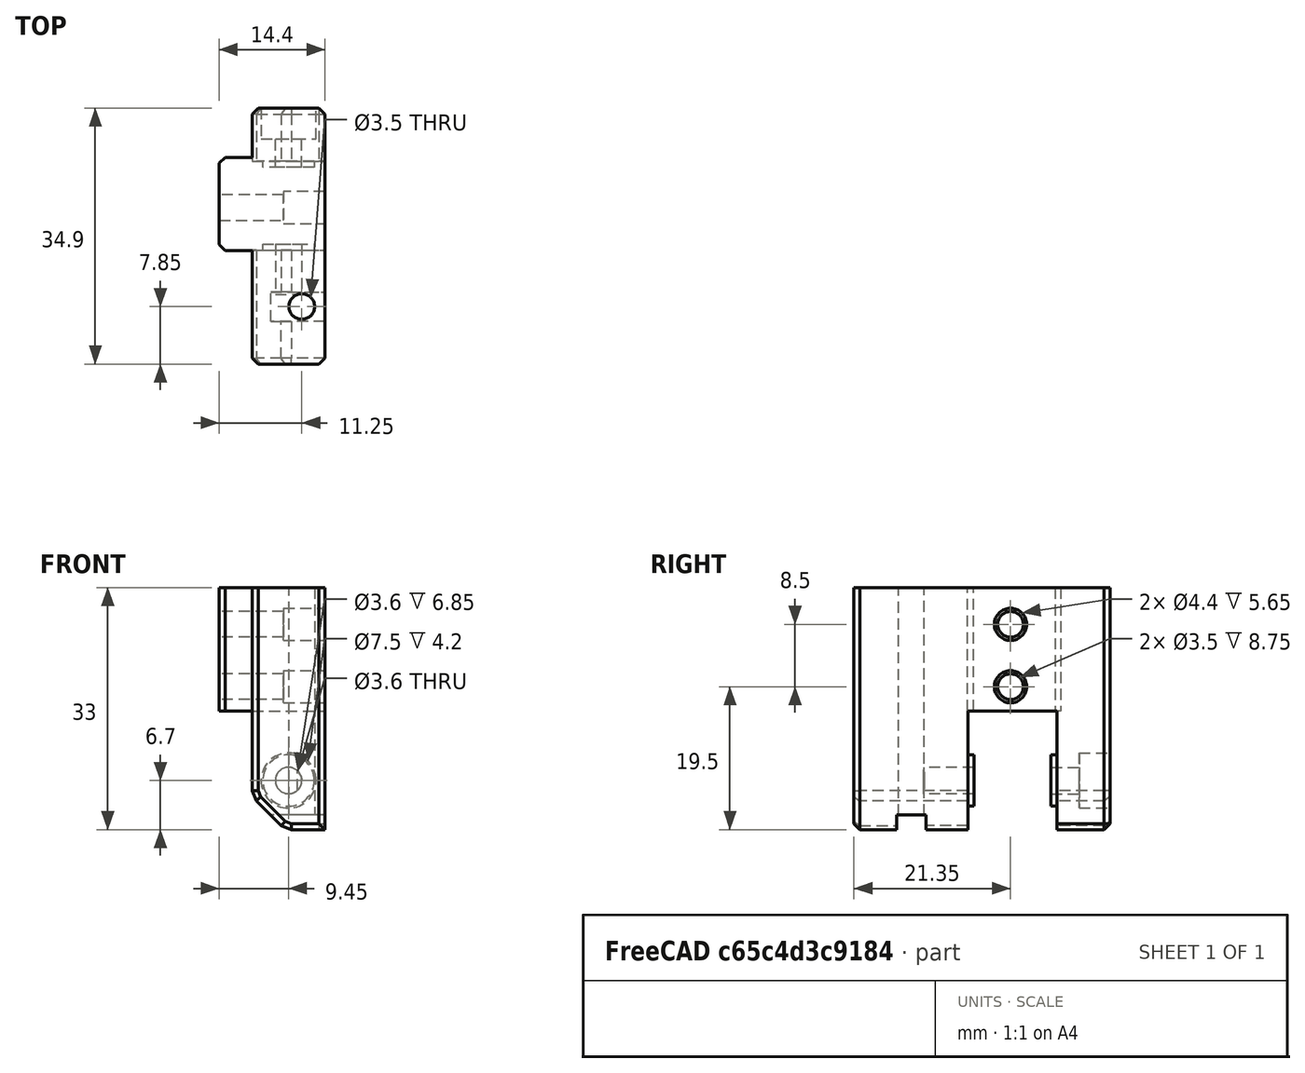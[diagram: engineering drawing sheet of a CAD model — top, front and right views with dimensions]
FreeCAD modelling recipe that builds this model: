
FCSTD DOCUMENT  (FreeCAD 1.0R38641 +468 (Git))
Label: k1_tensioner_left
License: All rights reserved
LicenseURL: https://en.wikipedia.org/wiki/All_rights_reserved
objects: Part::Feature×1, PartDesign::FeatureBase×1, PartDesign::Body×1, App::Link×1, App::Part×1
note: 4 computed .brp shape members not serialized (recipe doc carries the construction recipe); baked Part::Feature solids carry a one-line shape summary decoded from their .brp
EXTERNAL_REF file=cad_powge_pulley.FCStd obj=Part

FEATURE [Part::Feature] Part__Feature  label="step"
  shape: bbox 14.4 x 34.9 x 33 mm, 57 faces (baked)
FEATURE [PartDesign::FeatureBase] BaseFeature
  BaseFeature = -> Part__Feature
  Suppressed = false
FEATURE [PartDesign::Body] Body  label="k1_tensioner_left"
  AllowCompound = false
  BaseFeature = -> Part__Feature
  Group = -> [BaseFeature]
  Origin = -> Origin001
  Tip = -> BaseFeature
FEATURE [App::Link] Link  label="cad_powge_pulley_link"
  LinkPlacement = pos=(5.2,-18.65,6.7) rot=(-1,0,0;1.5708rad)
  LinkedObject = -> <external cad_powge_pulley.FCStd>#Part
  Placement = pos=(5.2,-18.65,6.7) rot=(-1,0,0;1.5708rad)
FEATURE [App::Part] Part  label="k1_tensioner_left_part"
  Group = -> [Body,Link]
  Origin = -> Origin
  Placement = pos=(0,0,0) rot=(0.57735,0.57735,0.57735;2.0944rad)

RESOLVED EXTERNAL PARTS (link-assembly join: the EXTERNAL_REF files above that resolve inside this repo's crawl, each included once):
---- part cad_powge_pulley.FCStd = doc fcstd_d49da9a9e340 ----
FCSTD DOCUMENT  (FreeCAD 1.0R38641 +468 (Git))
Label: cad_powge_pulley
License: All rights reserved
LicenseURL: https://en.wikipedia.org/wiki/All_rights_reserved
objects: Sketcher::SketchObject×1, PartDesign::Revolution×1, PartDesign::Body×1, App::Part×1
note: 6 computed .brp shape members not serialized (recipe doc carries the construction recipe); baked Part::Feature solids carry a one-line shape summary decoded from their .brp

FEATURE [Sketcher::SketchObject] Sketch
  ArcFitTolerance = 1e-06
  AttachmentSupport = -> [XZ_Plane]
  FullyConstrained = true
  MakeInternals = false
  MapMode = 5
  Placement = pos=(0,0,0) rot=(1,0,0;1.5708rad)
  sketch-geometry (8):
    g0: LineSegment StartX=6.1 StartY=9.3 StartZ=0 EndX=6.1 EndY=1.2 EndZ=0
    g1: LineSegment StartX=6.1 StartY=1.2 StartZ=0 EndX=8 EndY=1.2 EndZ=0
    g2: LineSegment StartX=8 StartY=1.2 StartZ=0 EndX=8 EndY=0 EndZ=0
    g3: LineSegment StartX=8 StartY=0 StartZ=0 EndX=2 EndY=0 EndZ=0
    g4: LineSegment StartX=2 StartY=0 StartZ=0 EndX=2 EndY=10.5 EndZ=0
    g5: LineSegment StartX=2 StartY=10.5 StartZ=0 EndX=8 EndY=10.5 EndZ=0
    g6: LineSegment StartX=8 StartY=10.5 StartZ=0 EndX=8 EndY=9.3 EndZ=0
    g7: LineSegment StartX=8 StartY=9.3 StartZ=0 EndX=6.1 EndY=9.3 EndZ=0
  constraints (24):
    c: Vertical(g0)
    c: Coincident(g1,g0)
    c: Horizontal(g1)
    c: Coincident(g2,g1)
    c: PointOnObject(g2,g-1)
    c: Vertical(g2)
    c: Coincident(g3,g2)
    c: PointOnObject(g3,g-1)
    c: Coincident(g4,g3)
    c: Vertical(g4)
    c: Coincident(g5,g4)
    c: Horizontal(g5)
    c: Coincident(g6,g5)
    c: Vertical(g6)
    c: Coincident(g7,g6)
    c: Horizontal(g7)
    c: Coincident(g0,g7)
    c: Equal(g5,g3)
    c: Equal(g6,g2)
    c: Distance(g4,g-2) = 2
    c: Distance(g5,g-2) = 8
    c: DistanceY(g0,g0) = 8.1
    c: DistanceY(g4,g4) = 10.5
    c: Distance(g0,g-2) = 6.1
FEATURE [PartDesign::Revolution] Revolution
  Angle = 360
  Angle2 = 60
  Axis = (0,2e-16,1)
  Base = (0,0,0)
  Placement = pos=(0,0,0) rot=(1,0,0;1.5708rad)
  Profile = -> Sketch
  ReferenceAxis = -> Sketch [V_Axis]
  Refine = true
  Reversed = true
  Suppressed = false
  Type = 0
FEATURE [PartDesign::Body] Body  label="powge_pulley"
  AllowCompound = false
  Group = -> [Sketch,Revolution]
  Origin = -> Origin
  Tip = -> Revolution
FEATURE [App::Part] Part  label="powge_pulley_part"
  Group = -> [Body]
  Origin = -> Origin001
